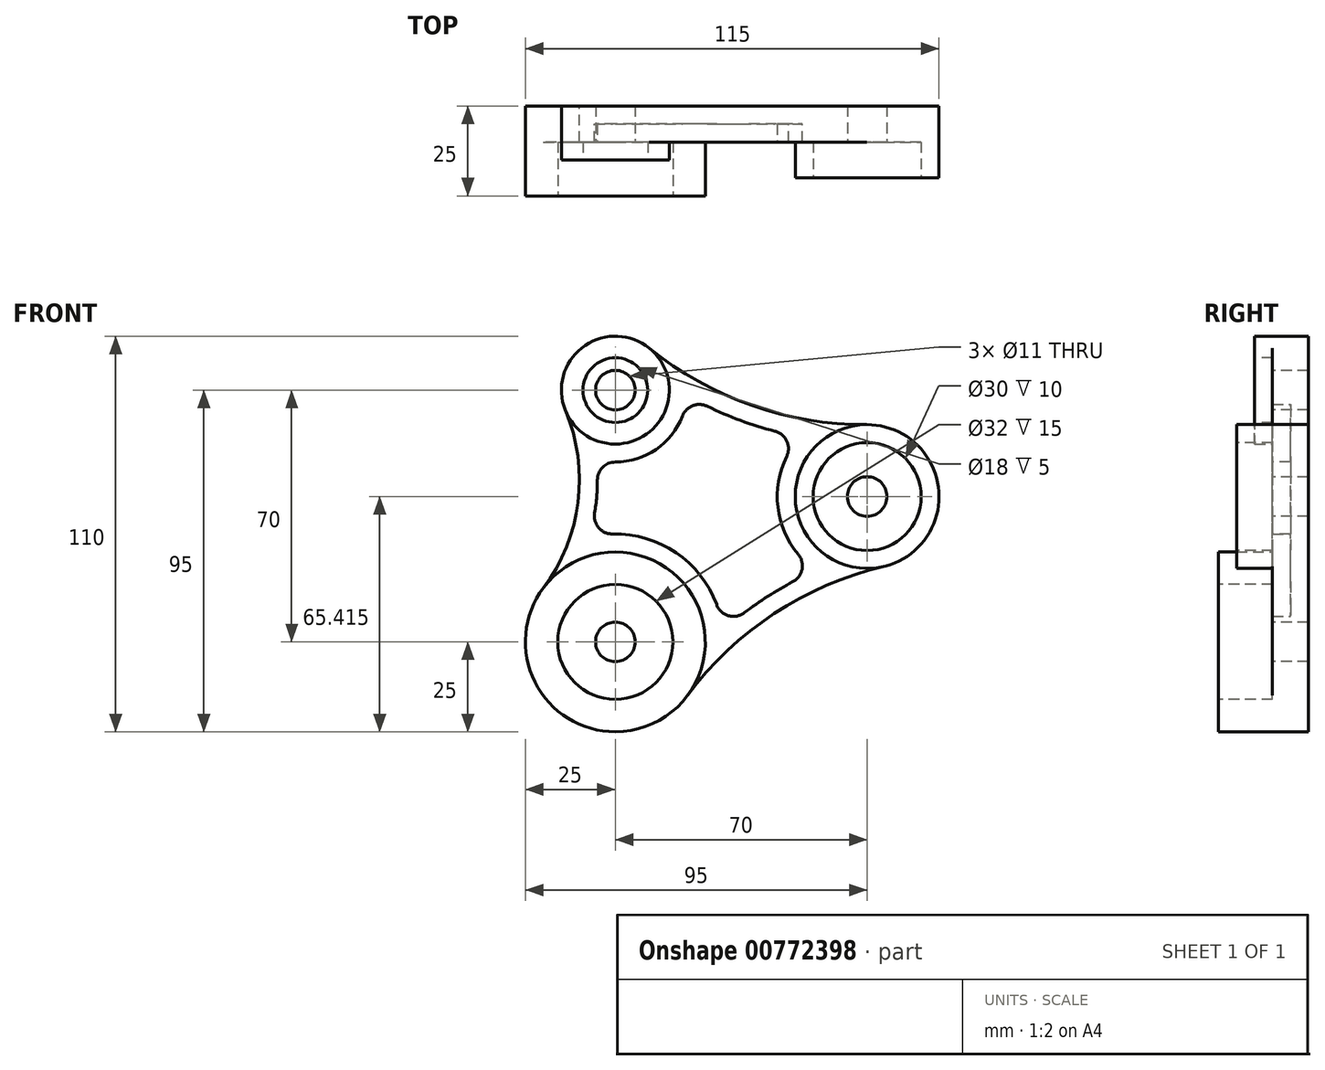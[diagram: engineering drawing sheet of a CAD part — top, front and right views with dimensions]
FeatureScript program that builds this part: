
annotation { "Feature Type Name" : "Feature", "Feature Type Description" : "" }
export const myFeature = defineFeature(function(context is Context, id is Id, definition is map)
    precondition{}
    {
        {
            var Q0;
            Q0=qCreatedBy(makeId("Front.planeOp"),FACE);
            var sketch = newSketch(context, id + "F0", { "sketchPlane" : qUnion([Q0])});
            skCircle(sketch, "E0", {"center": v(0, 0) * mm, "radius": 25 * mm});
            skCircle(sketch, "E1", {"center": v(70, 40.41) * mm, "radius": 20 * mm});
            skCircle(sketch, "E2", {"center": v(0, 70) * mm, "radius": 15 * mm});
            skLineSegment(sketch, "E3", {"start": v(70, 40.41) * mm, "end": v(0, 0) * mm, "construction": true});
            skLineSegment(sketch, "E4", {"start": v(0, 0) * mm, "end": v(73.1, 0) * mm, "construction": true});
            skArc(sketch, "E5", {"start": v(-20, 15) * mm, "mid": v(-10.39, 38.8) * mm, "end": v(-13.85, 64.23) * mm});
            skArc(sketch, "E6", {"start": v(9.45, 81.65) * mm, "mid": v(37.82, 65.78) * mm, "end": v(69.88, 60.41) * mm});
            skArc(sketch, "E7", {"start": v(74.58, 20.95) * mm, "mid": v(44.15, 7.85) * mm, "end": v(20.07, -14.9) * mm});
            skSolve(sketch);
        }
        {
            var Q0;
            {var subQ0=sQuery(id+"F0.wireOp",EDGE,"E5");Q0=makeQuery(id+"F0.imprint","IMPRINT",FACE,{"disambiguationData":[TD([[makeQuery(id+"F0.imprint","IMPRINT",EDGE,{"derivedFrom":subQ0}),-1.0]])]});}
            extrude(context, id + "F1", {"entities" : qUnion([Q0]), "depth" : 10 * mm, "offsetDistance" : 25 * mm});
        }
        {
            var Q0;
            {var subQ0=sQuery(id+"F0.wireOp",EDGE,"E2");var subQ1=makeQuery(id+"F0.imprint","INTERSECT",VERTEX,{"derivedFrom":[subQ0,sQuery(id+"F0.wireOp",EDGE,"E5")]});Q0=makeQuery(id+"F0.imprint","IMPRINT",FACE,{"disambiguationData":[TD([[makeQuery(id+"F0.imprint","IMPRINT",EDGE,{"disambiguationData":[TD([[subQ1,1.0]])],"derivedFrom":subQ0}),1.0]])]});}
            extrude(context, id + "F2", {"entities" : qUnion([Q0]), "operationType" : NewBodyOperationType.ADD, "depth" : 15 * mm, "offsetDistance" : 25 * mm});
        }
        {
            var Q0;
            {var subQ0=sQuery(id+"F0.wireOp",EDGE,"E0");var subQ1=makeQuery(id+"F0.imprint","INTERSECT",VERTEX,{"derivedFrom":[subQ0,sQuery(id+"F0.wireOp",EDGE,"E5")]});Q0=makeQuery(id+"F0.imprint","IMPRINT",FACE,{"disambiguationData":[TD([[makeQuery(id+"F0.imprint","IMPRINT",EDGE,{"disambiguationData":[TD([[subQ1,-1.0]])],"derivedFrom":subQ0}),1.0]])]});}
            extrude(context, id + "F3", {"entities" : qUnion([Q0]), "operationType" : NewBodyOperationType.ADD, "depth" : 25 * mm, "offsetDistance" : 25 * mm});
        }
        {
            var Q0;
            {var subQ0=sQuery(id+"F0.wireOp",EDGE,"E1");var subQ1=makeQuery(id+"F0.imprint","INTERSECT",VERTEX,{"derivedFrom":[subQ0,sQuery(id+"F0.wireOp",EDGE,"E6")]});Q0=makeQuery(id+"F0.imprint","IMPRINT",FACE,{"disambiguationData":[TD([[makeQuery(id+"F0.imprint","IMPRINT",EDGE,{"disambiguationData":[TD([[subQ1,-1.0]])],"derivedFrom":subQ0}),1.0]])]});}
            extrude(context, id + "F4", {"entities" : qUnion([Q0]), "operationType" : NewBodyOperationType.ADD, "depth" : 20 * mm, "offsetDistance" : 25 * mm});
        }
        {
            var Q0;
            Q0=makeQuery(id+"F3.opExtrude","CAP_FACE",FACE,{"disambiguationData":[OSD([sQuery(id+"F0.wireOp",EDGE,"E0")])],"isStart":false});
            var sketch = newSketch(context, id + "F5", { "sketchPlane" : qUnion([Q0])});
            skCircle(sketch, "E8", {"center": v(0, 0) * mm, "radius": 16 * mm});
            skCircle(sketch, "E9", {"center": v(0, 70) * mm, "radius": 9 * mm});
            skCircle(sketch, "E10", {"center": v(70, 40.41) * mm, "radius": 15 * mm});
            skSolve(sketch);
        }
        {
            var Q0;
            Q0=qSketchRegion(id+"F5",true);
            extrude(context, id + "F6", {"entities" : qUnion([Q0]), "operationType" : NewBodyOperationType.REMOVE, "oppositeDirection" : true, "depth" : 15 * mm, "offsetDistance" : 25 * mm});
        }
        {
            var Q0;
            Q0=makeQuery(id+"F6.boolean.opBoolean","COPY",FACE,{"derivedFrom":makeQuery(id+"F6.opExtrude","CAP_FACE",FACE,{"disambiguationData":[OSD([sQuery(id+"F5.wireOp",EDGE,"E8")])],"isStart":false})});
            var sketch = newSketch(context, id + "F7", { "sketchPlane" : qUnion([Q0])});
            skCircle(sketch, "E11", {"center": v(0, 0) * mm, "radius": 5.5 * mm});
            skCircle(sketch, "E12", {"center": v(0, 70) * mm, "radius": 5.5 * mm});
            skCircle(sketch, "E13", {"center": v(70, 40.41) * mm, "radius": 5.5 * mm});
            skSolve(sketch);
        }
        {
            var Q0;
            Q0=qSketchRegion(id+"F7",true);
            extrude(context, id + "F8", {"entities" : qUnion([Q0]), "operationType" : NewBodyOperationType.REMOVE, "endBound" : BoundingType.THROUGH_ALL, "oppositeDirection" : true, "depth" : 25 * mm, "offsetDistance" : 25 * mm});
        }
        {
            var Q0;
            Q0=makeQuery(id+"F1.opExtrude","CAP_FACE",FACE,{"disambiguationData":[OSD([sQuery(id+"F0.wireOp",EDGE,"E0"),sQuery(id+"F0.wireOp",EDGE,"E1"),sQuery(id+"F0.wireOp",EDGE,"E2"),sQuery(id+"F0.wireOp",EDGE,"E5"),sQuery(id+"F0.wireOp",EDGE,"E6"),sQuery(id+"F0.wireOp",EDGE,"E7")])],"isStart":false});
            var sketch = newSketch(context, id + "F9", { "sketchPlane" : qUnion([Q0])});
            skArc(sketch, "E14.0", {"start": v(-20, 15) * mm, "mid": v(-10.39, 38.8) * mm, "end": v(-13.85, 64.23) * mm, "construction": true});
            skArc(sketch, "E15.0", {"start": v(-13.85, 64.23) * mm, "mid": v(8.98, 57.99) * mm, "end": v(9.45, 81.65) * mm, "construction": true});
            skArc(sketch, "E16.0", {"start": v(9.45, 81.65) * mm, "mid": v(37.82, 65.78) * mm, "end": v(69.88, 60.41) * mm, "construction": true});
            skArc(sketch, "E17.0", {"start": v(69.88, 60.41) * mm, "mid": v(50.14, 38.05) * mm, "end": v(74.58, 20.95) * mm, "construction": true});
            skArc(sketch, "E18.0", {"start": v(20.07, -14.9) * mm, "mid": v(14.95, 20.04) * mm, "end": v(-20, 15) * mm, "construction": true});
            skArc(sketch, "E19.0", {"start": v(74.58, 20.95) * mm, "mid": v(44.15, 7.85) * mm, "end": v(20.07, -14.9) * mm, "construction": true});
            skArc(sketch, "E20.0", {"start": v(19.94, 68.45) * mm, "mid": v(35.16, 61.43) * mm, "end": v(51.33, 57.04) * mm});
            skArc(sketch, "E20.1", {"start": v(55.76, 19.87) * mm, "mid": v(42.15, 12.5) * mm, "end": v(29.84, 3.14) * mm});
            skArc(sketch, "E20.2", {"start": v(29.84, 3.14) * mm, "mid": v(17.16, 24.6) * mm, "end": v(-7.35, 29.08) * mm});
            skArc(sketch, "E20.3", {"start": v(51.33, 57.04) * mm, "mid": v(45.18, 37.46) * mm, "end": v(55.76, 19.87) * mm});
            skArc(sketch, "E20.4", {"start": v(-7.35, 29.08) * mm, "mid": v(-5.25, 39.8) * mm, "end": v(-5.3, 50.71) * mm});
            skArc(sketch, "E20.5", {"start": v(-5.3, 50.71) * mm, "mid": v(11.5, 53.64) * mm, "end": v(19.94, 68.45) * mm});
            skSolve(sketch);
        }
        {
            var Q0;
            Q0=qSketchRegion(id+"F9",true);
            extrude(context, id + "F10", {"entities" : qUnion([Q0]), "operationType" : NewBodyOperationType.REMOVE, "oppositeDirection" : true, "depth" : 5 * mm, "offsetDistance" : 25 * mm});
        }
        {
            var Q0;
            Q0=makeQuery(id+"F10.boolean.opBoolean","COPY",EDGE,{"derivedFrom":makeQuery(id+"F10.opExtrude","SWEPT_EDGE",EDGE,{"disambiguationData":[OSD([sQuery(id+"F9.wireOp",EDGE,"E20.0"),sQuery(id+"F9.wireOp",EDGE,"E20.5")])]})});
            var Q1;
            Q1=makeQuery(id+"F10.boolean.opBoolean","COPY",EDGE,{"derivedFrom":makeQuery(id+"F10.opExtrude","SWEPT_EDGE",EDGE,{"disambiguationData":[OSD([sQuery(id+"F9.wireOp",EDGE,"E20.4"),sQuery(id+"F9.wireOp",EDGE,"E20.5")])]})});
            var Q2;
            Q2=makeQuery(id+"F10.boolean.opBoolean","COPY",EDGE,{"derivedFrom":makeQuery(id+"F10.opExtrude","SWEPT_EDGE",EDGE,{"disambiguationData":[OSD([sQuery(id+"F9.wireOp",EDGE,"E20.0"),sQuery(id+"F9.wireOp",EDGE,"E20.3")])]})});
            var Q3;
            Q3=makeQuery(id+"F10.boolean.opBoolean","COPY",EDGE,{"derivedFrom":makeQuery(id+"F10.opExtrude","SWEPT_EDGE",EDGE,{"disambiguationData":[OSD([sQuery(id+"F9.wireOp",EDGE,"E20.1"),sQuery(id+"F9.wireOp",EDGE,"E20.3")])]})});
            var Q4;
            Q4=makeQuery(id+"F10.boolean.opBoolean","COPY",EDGE,{"derivedFrom":makeQuery(id+"F10.opExtrude","SWEPT_EDGE",EDGE,{"disambiguationData":[OSD([sQuery(id+"F9.wireOp",EDGE,"E20.2"),sQuery(id+"F9.wireOp",EDGE,"E20.4")])]})});
            var Q5;
            Q5=makeQuery(id+"F10.boolean.opBoolean","COPY",EDGE,{"derivedFrom":makeQuery(id+"F10.opExtrude","SWEPT_EDGE",EDGE,{"disambiguationData":[OSD([sQuery(id+"F9.wireOp",EDGE,"E20.1"),sQuery(id+"F9.wireOp",EDGE,"E20.2")])]})});
            fillet(context, id + "F11", {"entities" : qUnion([Q0, Q1, Q2, Q3, Q4, Q5]), "radius" : 5 * mm, "tangentPropagation" : true, "allowEdgeOverflow" : false});
        }
    });
